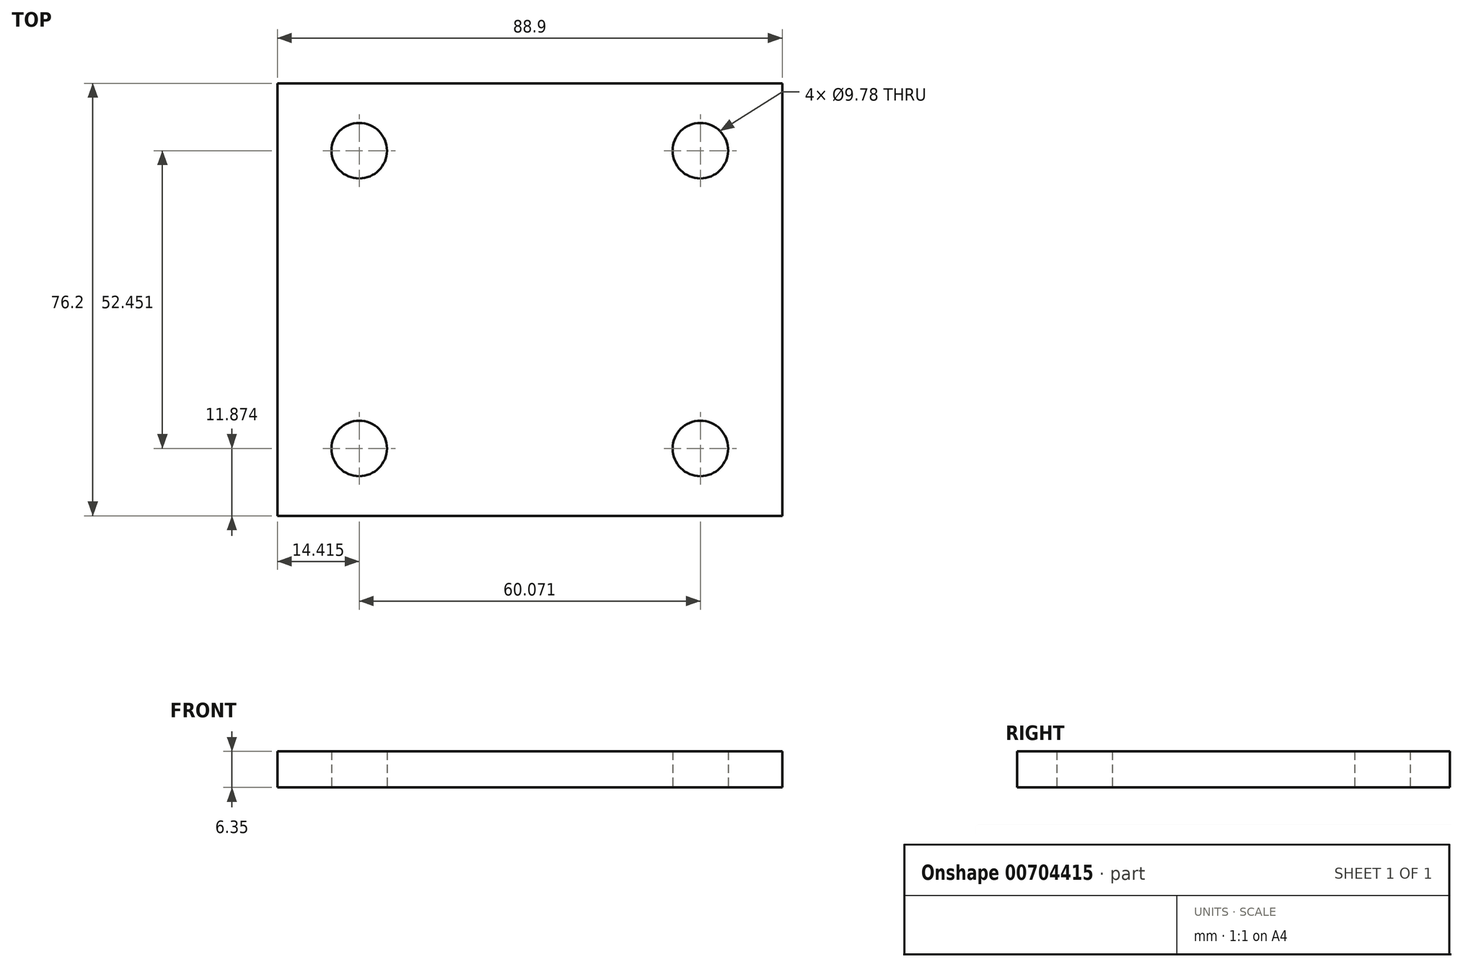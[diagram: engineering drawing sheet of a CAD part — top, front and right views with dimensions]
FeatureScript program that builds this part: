
annotation { "Feature Type Name" : "Feature", "Feature Type Description" : "" }
export const myFeature = defineFeature(function(context is Context, id is Id, definition is map)
    precondition{}
    {
        {
            var Q0;
            Q0=qCreatedBy(makeId("Top.planeOp"),FACE);
            var sketch = newSketch(context, id + "F0", { "sketchPlane" : qUnion([Q0])});
            skLineSegment(sketch, "E0.bottom", {"start": v(0, 0) * mm, "end": v(88.9, 0) * mm});
            skLineSegment(sketch, "E0.top", {"start": v(0, 76.2) * mm, "end": v(88.9, 76.2) * mm});
            skLineSegment(sketch, "E0.left", {"start": v(0, 0) * mm, "end": v(0, 76.2) * mm});
            skLineSegment(sketch, "E0.right", {"start": v(88.9, 0) * mm, "end": v(88.9, 76.2) * mm});
            skLineSegment(sketch, "E1", {"start": v(44.45, 76.2) * mm, "end": v(44.45, 0) * mm, "construction": true});
            skLineSegment(sketch, "E2", {"start": v(0, 38.1) * mm, "end": v(88.9, 38.1) * mm, "construction": true});
            skCircle(sketch, "E3", {"center": v(14.41, 64.33) * mm, "radius": 4.89 * mm});
            skCircle(sketch, "E4.MirrorC", {"center": v(14.41, 11.87) * mm, "radius": 4.89 * mm});
            skCircle(sketch, "E5.MirrorC", {"center": v(74.49, 64.33) * mm, "radius": 4.89 * mm});
            skCircle(sketch, "E6.MirrorC", {"center": v(74.49, 11.87) * mm, "radius": 4.89 * mm});
            skSolve(sketch);
        }
        {
            var Q0;
            Q0 = qSketchRegion(id + "F0", true);
            extrude(context, id + "F1", {"entities" : qUnion([Q0]), "depth" : 6.35 * mm, "offsetDistance" : 25.4 * mm});
        }
    });
